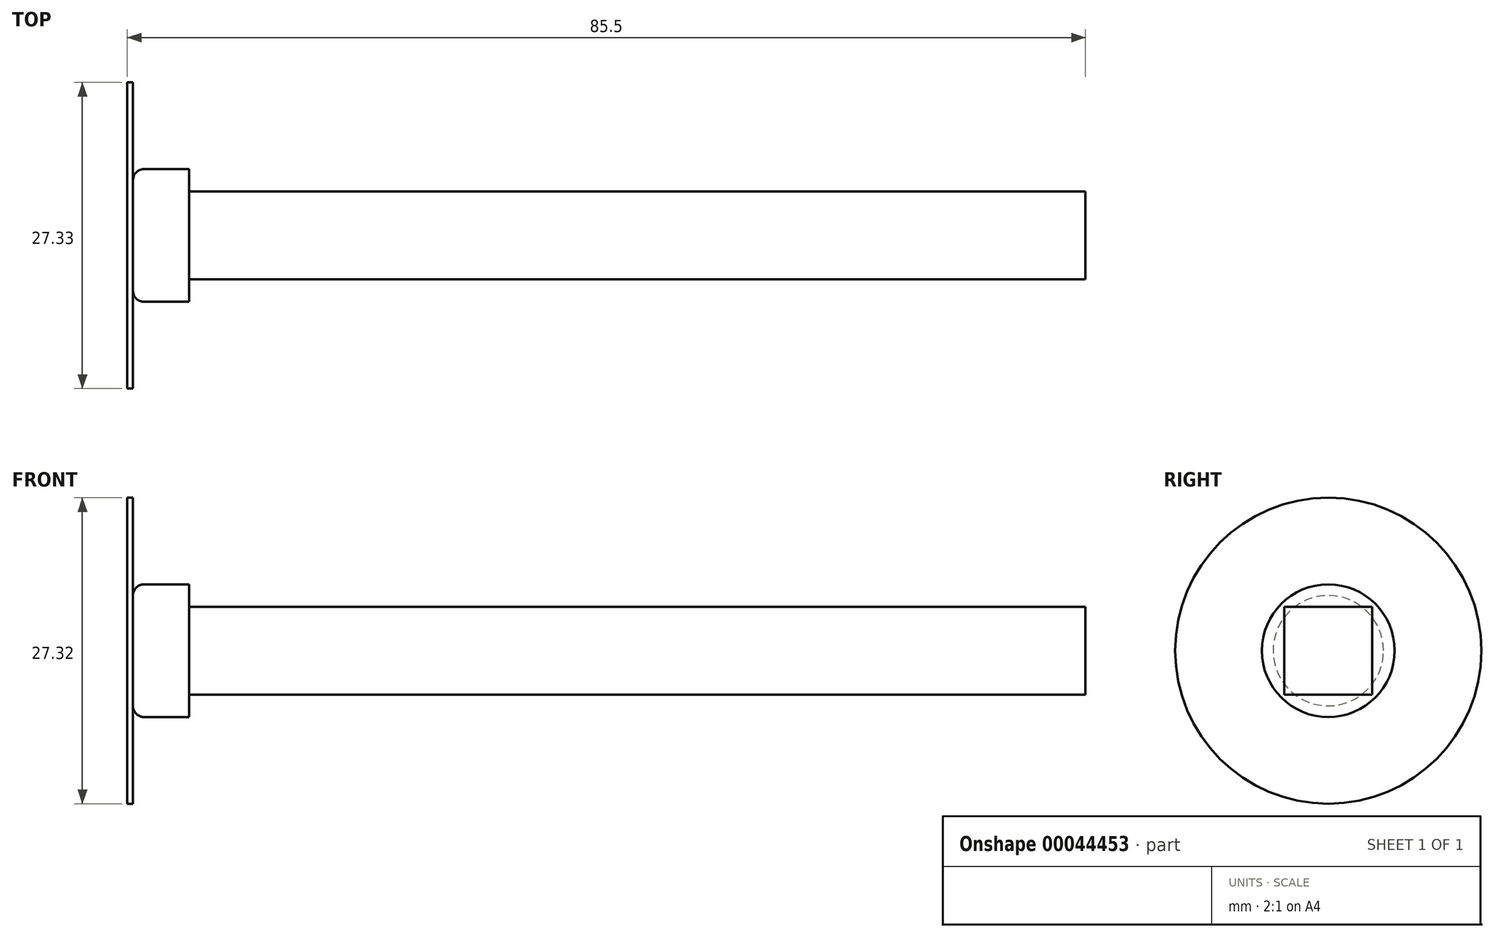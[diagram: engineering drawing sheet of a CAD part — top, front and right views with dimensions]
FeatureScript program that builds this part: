
annotation { "Feature Type Name" : "Feature", "Feature Type Description" : "" }
export const myFeature = defineFeature(function(context is Context, id is Id, definition is map)
    precondition{}
    {
        {
            var Q0;
            Q0=qCreatedBy(makeId("Right.planeOp"),FACE);
            var sketch = newSketch(context, id + "F0", { "sketchPlane" : qUnion([Q0])});
            skLineSegment(sketch, "E0.rect.bottom", {"start": v(20, -3.93) * mm, "end": v(12.15, -3.93) * mm});
            skLineSegment(sketch, "E0.rect.top", {"start": v(20, 3.92) * mm, "end": v(12.15, 3.92) * mm});
            skLineSegment(sketch, "E0.rect.left", {"start": v(20, -3.93) * mm, "end": v(20, 3.93) * mm});
            skLineSegment(sketch, "E0.rect.right", {"start": v(12.15, -3.93) * mm, "end": v(12.15, 3.92) * mm});
            skPoint(sketch, "E0.rect.middle", {"position": v(16.07, 0) * mm});
            skSolve(sketch);
        }
        {
            var Q0;
            Q0=makeQuery(id+"F0.imprint","IMPRINT",FACE,{"disambiguationData":[TD([[makeQuery(id+"F0.imprint","IMPRINT",EDGE,{"derivedFrom":sQuery(id+"F0.wireOp",EDGE,"E0.rect.bottom")}),-1.0]])]});
            extrude(context, id + "F1", {"entities" : qUnion([Q0]), "depth" : 85 * mm});
        }
        {
            var Q0;
            Q0=makeQuery(id+"F1.opExtrude","CAP_FACE",FACE,{"disambiguationData":[OSD([sQuery(id+"F0.wireOp",EDGE,"E0.rect.bottom"),sQuery(id+"F0.wireOp",EDGE,"E0.rect.top"),sQuery(id+"F0.wireOp",EDGE,"E0.rect.left"),sQuery(id+"F0.wireOp",EDGE,"E0.rect.right")])],"isStart":true});
            var sketch = newSketch(context, id + "F2", { "sketchPlane" : qUnion([Q0])});
            skLineSegment(sketch, "E1", {"start": v(-16.07, 3.92) * mm, "end": v(-16.07, -3.92) * mm});
            skLineSegment(sketch, "E2", {"start": v(-12.15, 0) * mm, "end": v(-20, 0) * mm});
            skCircle(sketch, "E3", {"center": v(-16.07, 0) * mm, "radius": 5.92 * mm});
            skSolve(sketch);
        }
        {
            var Q0;
            Q0=makeQuery(id+"F2.imprint","IMPRINT",FACE,{"disambiguationData":[TD([[makeQuery(id+"F2.imprint","IMPRINT",EDGE,{"derivedFrom":sQuery(id+"F2.wireOp",EDGE,"E3")}),1.0]])]});
            extrude(context, id + "F3", {"entities" : qUnion([Q0]), "operationType" : NewBodyOperationType.ADD, "oppositeDirection" : true, "depth" : 5 * mm});
        }
        {
            var Q0;
            Q0=makeQuery(id+"F3.opExtrude","CAP_EDGE",EDGE,{"disambiguationData":[OSD([sQuery(id+"F2.wireOp",EDGE,"E3")])],"isStart":true});
            fillet(context, id + "F4", {"entities" : qUnion([Q0]), "radius" : 1 * mm, "tangentPropagation" : true, "allowEdgeOverflow" : false});
        }
        {
            var Q0;
            {var subQ0=sQuery(id+"F0.wireOp",EDGE,"E0.rect.bottom");var subQ1=sQuery(id+"F0.wireOp",EDGE,"E0.rect.top");var subQ2=sQuery(id+"F0.wireOp",EDGE,"E0.rect.left");var subQ3=sQuery(id+"F0.wireOp",EDGE,"E0.rect.right");Q0=makeQuery(id+"F3.boolean.opBoolean","MERGE",FACE,{"derivedFrom":[makeQuery(id+"F1.opExtrude","CAP_FACE",FACE,{"disambiguationData":[OSD([subQ0,subQ1,subQ2,subQ3])],"isStart":true}),makeQuery(id+"F3.opExtrude","CAP_FACE",FACE,{"disambiguationData":[OSD([subQ0,subQ1,subQ2,subQ3,sQuery(id+"F2.wireOp",EDGE,"E3")])],"isStart":true})]});}
            var sketch = newSketch(context, id + "F5", { "sketchPlane" : qUnion([Q0])});
            skCircle(sketch, "E4", {"center": v(-16.07, 0) * mm, "radius": 13.66 * mm});
            skSolve(sketch);
        }
        {
            var Q0;
            Q0=makeQuery(id+"F5.imprint","IMPRINT",FACE,{"disambiguationData":[TD([[makeQuery(id+"F5.imprint","IMPRINT",EDGE,{"derivedFrom":sQuery(id+"F5.wireOp",EDGE,"E4")}),1.0]])]});
            var Q1;
            {var subQ0=sQuery(id+"F2.wireOp",EDGE,"E3");var subQ1=sQuery(id+"F0.wireOp",EDGE,"E0.rect.bottom");var subQ2=sQuery(id+"F0.wireOp",EDGE,"E0.rect.top");var subQ3=sQuery(id+"F0.wireOp",EDGE,"E0.rect.left");var subQ4=sQuery(id+"F0.wireOp",EDGE,"E0.rect.right");Q1=makeQuery(id+"F5.imprint","IMPRINT",FACE,{"disambiguationData":[TD([[makeQuery(id+"F5.imprint","IMPRINT",EDGE,{"derivedFrom":makeQuery(id+"F4.opFillet","BLEND_EDGE",EDGE,{"blendedFrom":[makeQuery(id+"F3.opExtrude","CAP_EDGE",EDGE,{"disambiguationData":[OSD([subQ0])],"isStart":true}),makeQuery(id+"F3.boolean.opBoolean","MERGE",FACE,{"derivedFrom":[makeQuery(id+"F1.opExtrude","CAP_FACE",FACE,{"disambiguationData":[OSD([subQ1,subQ2,subQ3,subQ4])],"isStart":true}),makeQuery(id+"F3.opExtrude","CAP_FACE",FACE,{"disambiguationData":[OSD([subQ1,subQ2,subQ3,subQ4,subQ0])],"isStart":true})]})],"blendedInto":[makeQuery(id+"F3.boolean.opBoolean","MERGE",FACE,{"derivedFrom":[makeQuery(id+"F1.opExtrude","CAP_FACE",FACE,{"disambiguationData":[OSD([subQ1,subQ2,subQ3,subQ4])],"isStart":true}),makeQuery(id+"F3.opExtrude","CAP_FACE",FACE,{"disambiguationData":[OSD([subQ1,subQ2,subQ3,subQ4,subQ0])],"isStart":true})]})]})}),1.0]])]});}
            extrude(context, id + "F6", {"entities" : qUnion([Q0, Q1]), "operationType" : NewBodyOperationType.ADD, "depth" : .5 * mm});
        }
    });
